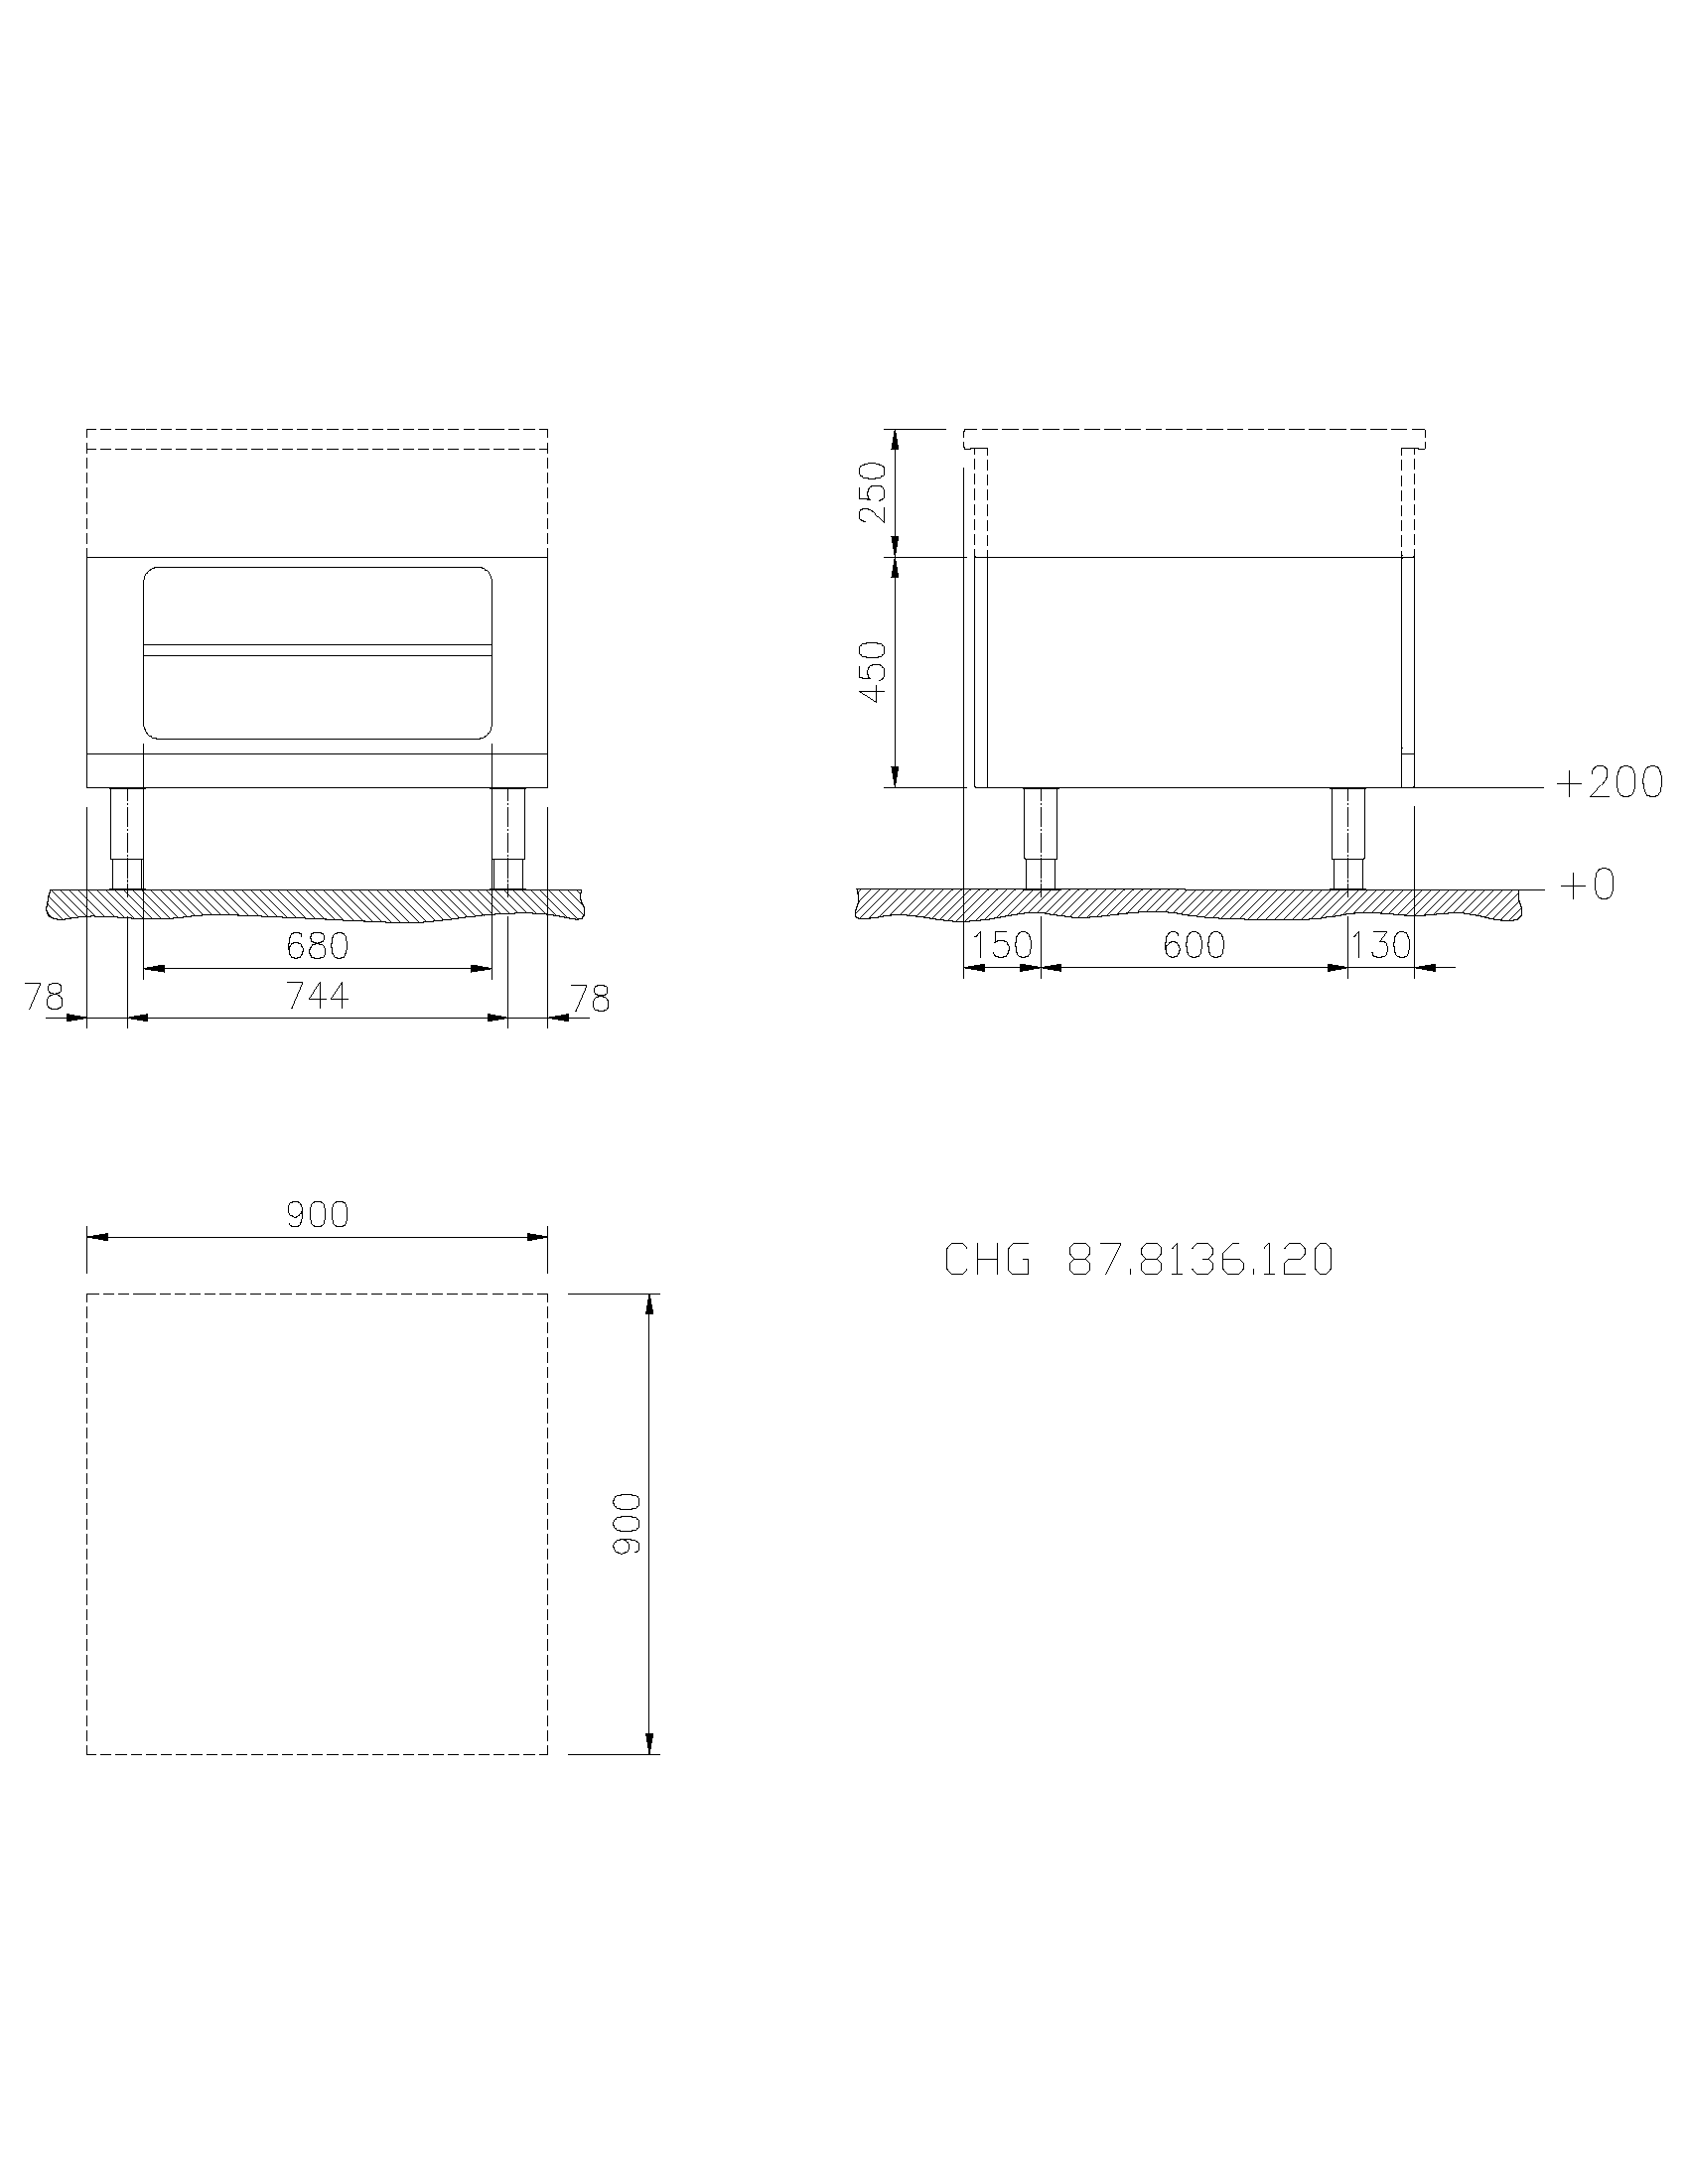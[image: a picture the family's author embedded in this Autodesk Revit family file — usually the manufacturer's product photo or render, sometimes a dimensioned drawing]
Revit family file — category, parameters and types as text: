
# Revit family: QF_ELECTROLUXPROFESSIONAL_589805_MC1HCAEOOM
name_source: partatom
category: Attrezzature speciali
units: mm (PartAtom-declared; Revit-internal decimal feet)

## family parameters
Basato su piano di lavoro = No
Condiviso = No
Punto di calcolo locali = No
Quota connettore circolare = Usa diametro
Sempre verticale = Sì
Taglio con vuoti quando caricato = No
Tipo di parte = Normale

## types (1)
- Standard
    Accessory = Sì
    Cold Water Size = 0"
    Compressed Air Pressure = 0.00 psi
    Compressed Air Size = 0"
    Compressed Air Volume = 0 GPM
    Condensate Return Size = 0"
    Cycle = 0 Hz
    Depth Actual = 900 mm  [stored 2.95276 ft]
    Descrizione = OPEN BASE,H3,GN,1S,500X900X450 MARINE
    Direct Waste Size = 0"
    Gas Input Pressure = 0.0
    Gas KW = 0
    Gas Size = 0"
    HP = 0 HP
    Height Actual = 450 mm  [stored 1.47638 ft]
    Hot Water Size = 0"
    Item Number = 589805
    Length Actual = 500 mm  [stored 1.64042 ft]
    Modello = MC1HCAEOOM
    Phase = 0
    Produttore = Electrolux Professional
    Prospetto di default = 0 mm  [stored 0 ft]
    Refrigerant Compressor Remote = Sì
    Refrigeration Liquid Line Size = 0 mm  [stored 0 ft]
    Refrigeration Suction Line Size = 0 mm  [stored 0 ft]
    Steam Consumption per Hour = 0
    Steam Supply Maximum Pressure = 0.00 psi
    Steam Supply Minimum Pressure = 0.00 psi
    Steam Supply Size = 0"
    URL = https://www.electroluxprofessional.com
    URL Manufacturer = https://www.electroluxprofessional.com
    Volts = 0 V
    Watts = 0 W
    Weight = 19.00 kg

note: source unit labels omitted for Gas Input Pressure — the stored unit's dimension contradicts the parameter name (converter mislabeling)

note: [stored X ft] marks values corroborated as IEEE doubles in the binary element streams (Revit-internal decimal feet)

## geometry (parser evidence)
native form markers: Blend x10, Sweep x3
no freeform markers — native parametric forms only
